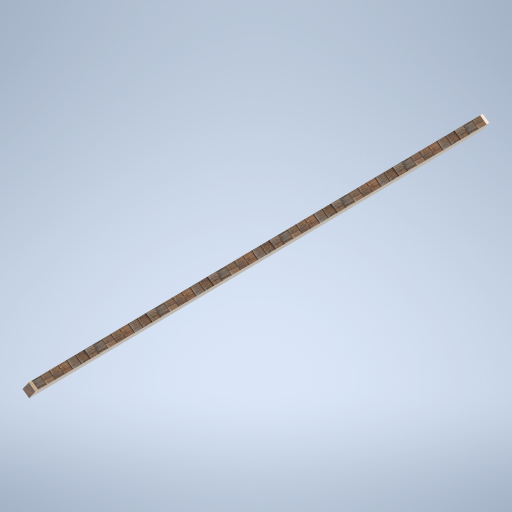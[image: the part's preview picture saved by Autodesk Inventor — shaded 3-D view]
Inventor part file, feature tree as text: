
AUTODESK INVENTOR PART (.ipt)
format: ipt  version: 2024.2 (Build 282272000, 272)  size: 303,104 bytes
history: native  units: in
note: dims shown in document units (in); Inventor stores cm internally (conversion verified against a paired STEP export)
features: sketch x5, other x3, plane x2
ambient origin geometry x8: Origin, YZ Plane, XZ Plane, XY Plane, X Axis, Y Axis, Z Axis, Center Point
bodies: Solid1 (feature_tree)
feature tree (10):
  other  "support_beam_segment_0106.ipt"
  other  "Solid1::support_beam_segment_0106.ipt"
  other  "TaggingFeature1"
  sketch  "Sketch1"  dims[d0=0.3937in]
  sketch  "Sketch2"
  sketch  "Sketch3"
  sketch  "Sketch4"
  sketch  "Sketch5"
  plane  "Work Plane1"
  plane  "Work Plane2"
